# Revit family: Power-ModularDevices-GEWISS-90AM-SPD_TYPE2_PHONE
name_source: partatom
category: Apparecchi elettrici
revit_build: Autodesk Revit 2016 (Build: 20161004_0715(x64)
units: mm (PartAtom-declared; Revit-internal decimal feet)

## family parameters
Condiviso = No
Host = Superficie
Mantenere orientamento annotazione = Sì
Numero OmniClass = 23.80.50.00
Punto di calcolo locali = Sì
Quota connettore circolare = Usa diametro
Taglio con vuoti quando caricato = No
Tipo di parte = Normale
Titolo OmniClass = Terminals for Power Supply

## types (1)
- GWD6430 - LST - SPD FOR PHONE LINE ADSL/PSTN
    Catalogue = POWER
    Catalogue Range = 90 AM
    Descrizione = LST - SPD FOR PHONE LINE ADSL/PSTN
    EAN code = 8011564775053
    Electrocod = 0641
    IDF = cbe7d0af-92f3-4a60-ab83-58e67a5db77d
    IDT = edf14c64-f18c-4414-8396-2d32234e7abe
    Immagine tipo = GWD6430.jpg
    Maximum discharge current: = 10KA
    Modello = GWD6430
    No. Chorus modules = 1
    No. of modules EN 50022 = 1
    Numero di poli = 1
    Produttore = GEWISS S.p.A.
    Prospetto di default = 1219 mm
    Rated voltage = 50Vac
    Rated voltage AC = 50V
    SEO = Limiter
    Spostamento_x = -340 mm
    Technical sheet = https://www.gewiss.com
    Type = Telephone/data lines
    Type: = Telephone/data lines
    URL = https://www.gewiss.com
    Version file RFA = 18.0
    carico = Altro
    potenza in watt = 0 V
